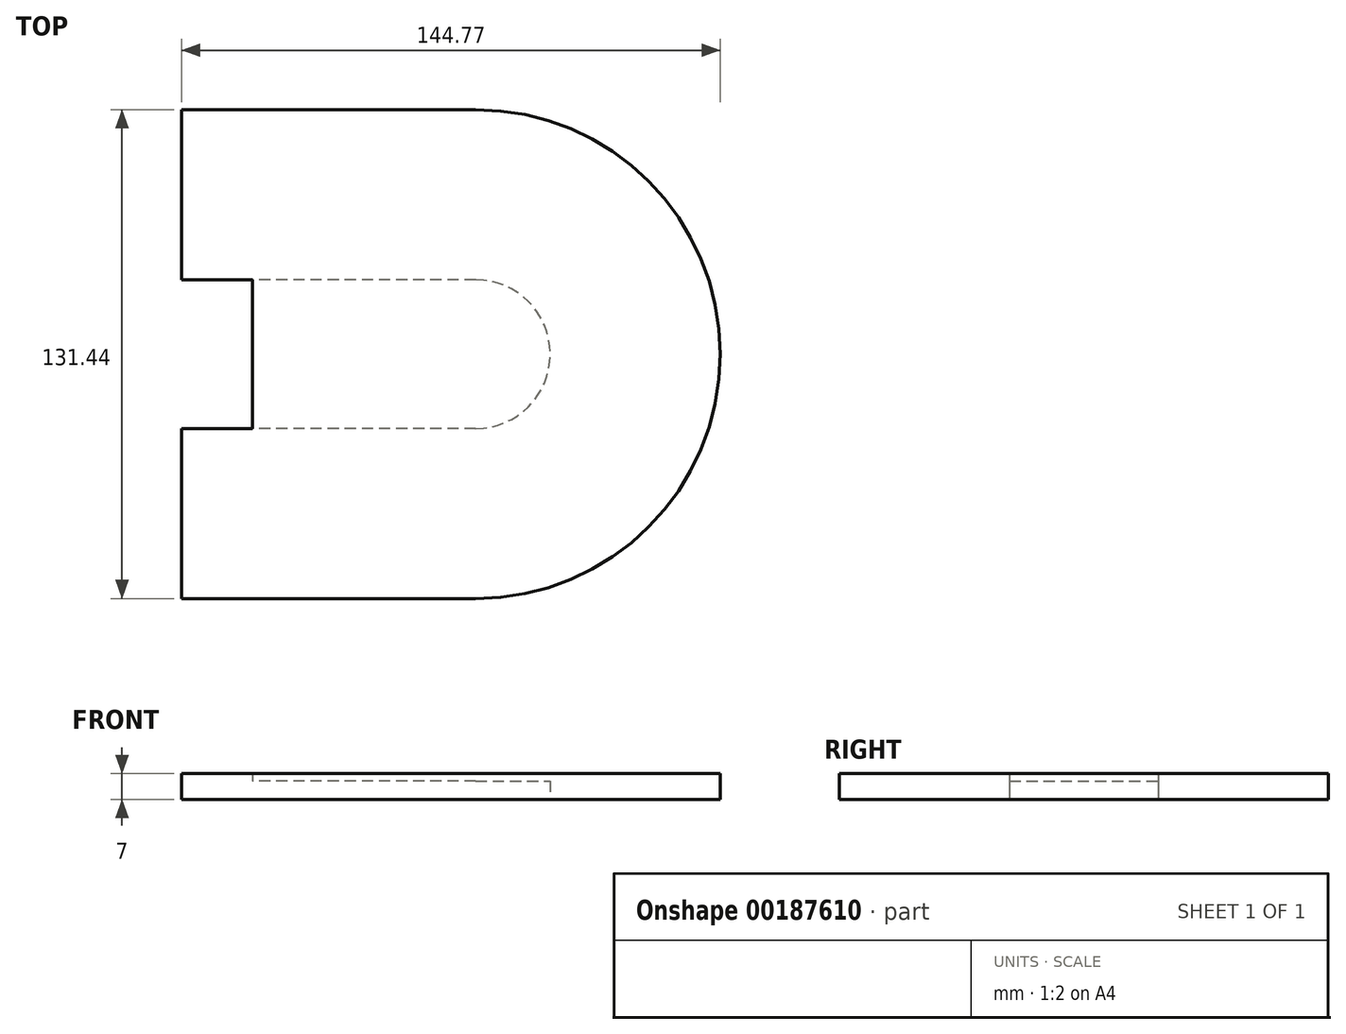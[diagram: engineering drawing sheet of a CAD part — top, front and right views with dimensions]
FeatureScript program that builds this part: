
annotation { "Feature Type Name" : "Feature", "Feature Type Description" : "" }
export const myFeature = defineFeature(function(context is Context, id is Id, definition is map)
    precondition{}
    {
        {
            var Q0;
            Q0=qCreatedBy(makeId("Top.planeOp"),FACE);
            var sketch = newSketch(context, id + "F0", { "sketchPlane" : qUnion([Q0])});
            skLineSegment(sketch, "E0.bottom", {"start": v(20, -20) * mm, "end": v(-40, -20) * mm});
            skLineSegment(sketch, "E0.top", {"start": v(20, 20) * mm, "end": v(-40, 20) * mm});
            skLineSegment(sketch, "E0.right", {"start": v(-40, -20) * mm, "end": v(-40, 20) * mm});
            skPoint(sketch, "E0.middle", {"position": v(0, 0) * mm});
            skArc(sketch, "E1", {"start": v(20, -20) * mm, "mid": v(40, 0) * mm, "end": v(20, 20) * mm});
            skPoint(sketch, "E2.orphan", {"position": v(40, 20) * mm});
            skPoint(sketch, "E3.orphan", {"position": v(40, -20) * mm});
            skLineSegment(sketch, "E4.0", {"start": v(20, 45.4) * mm, "end": v(-65.4, 45.4) * mm});
            skArc(sketch, "E4.1", {"start": v(20, -45.4) * mm, "mid": v(65.4, 0) * mm, "end": v(20, 45.4) * mm});
            skLineSegment(sketch, "E4.2", {"start": v(20, -45.4) * mm, "end": v(-65.4, -45.4) * mm});
            skLineSegment(sketch, "E4.3", {"start": v(-65.4, -45.4) * mm, "end": v(-65.4, 45.4) * mm});
            skLineSegment(sketch, "E5", {"start": v(-40, -45.4) * mm, "end": v(-40, 45.4) * mm});
            skSolve(sketch);
        }
        {
            var Q0;
            {var subQ4=sQuery(id+"F0.wireOp",EDGE,"E0.bottom");Q0=makeQuery(id+"F0.imprint","IMPRINT",FACE,{"disambiguationData":[TD([[makeQuery(id+"F0.imprint","IMPRINT",EDGE,{"derivedFrom":subQ4}),1.0]])]});}
            var Q1;
            {var subQ0=sQuery(id+"F0.wireOp",EDGE,"E0.bottom");Q1=makeQuery(id+"F0.imprint","IMPRINT",FACE,{"disambiguationData":[TD([[makeQuery(id+"F0.imprint","IMPRINT",EDGE,{"derivedFrom":subQ0}),-1.0]])]});}
            extrude(context, id + "F1", {"entities" : qUnion([Q0, Q1]), "depth" : 7 * mm});
        }
        {
            var Q0;
            {var subQ0=sQuery(id+"F0.wireOp",EDGE,"E0.bottom");Q0=makeQuery(id+"F0.imprint","IMPRINT",FACE,{"disambiguationData":[TD([[makeQuery(id+"F0.imprint","IMPRINT",EDGE,{"derivedFrom":subQ0}),-1.0]])]});}
            extrude(context, id + "F2", {"entities" : qUnion([Q0]), "operationType" : NewBodyOperationType.REMOVE, "depth" : 5 * mm});
        }
        {
            var Q0;
            Q0=makeQuery(id+"F1.opExtrude","SWEPT_FACE",FACE,{"disambiguationData":[OSD([sQuery(id+"F0.wireOp",EDGE,"E5")])]});
            var sketch = newSketch(context, id + "F3", { "sketchPlane" : qUnion([Q0])});
            skLineSegment(sketch, "E6.bottom", {"start": v(-45.4, 7) * mm, "end": v(-20, 7) * mm});
            skLineSegment(sketch, "E6.top", {"start": v(-45.4, 0) * mm, "end": v(-20, 0) * mm});
            skLineSegment(sketch, "E6.left", {"start": v(-45.4, 7) * mm, "end": v(-45.4, 0) * mm});
            skLineSegment(sketch, "E6.right", {"start": v(-20, 7) * mm, "end": v(-20, 0) * mm});
            skLineSegment(sketch, "E7.bottom", {"start": v(45.4, 7) * mm, "end": v(20, 7) * mm});
            skLineSegment(sketch, "E7.top", {"start": v(45.4, 0) * mm, "end": v(20, 0) * mm});
            skLineSegment(sketch, "E7.left", {"start": v(45.4, 7) * mm, "end": v(45.4, 0) * mm});
            skLineSegment(sketch, "E7.right", {"start": v(20, 7) * mm, "end": v(20, 0) * mm});
            skSolve(sketch);
        }
        {
            var Q0;
            Q0 = qSketchRegion(id + "F3", true);
            extrude(context, id + "F4", {"entities" : qUnion([Q0]), "operationType" : NewBodyOperationType.ADD, "depth" : 19.05 * mm});
        }
        {
            var Q0;
            Q0=makeQuery(id+"F4.boolean.opBoolean","MERGE",FACE,{"derivedFrom":[makeQuery(id+"F1.opExtrude","CAP_FACE",FACE,{"disambiguationData":[OSD([sQuery(id+"F0.wireOp",EDGE,"E4.0"),sQuery(id+"F0.wireOp",EDGE,"E4.1"),sQuery(id+"F0.wireOp",EDGE,"E4.2"),sQuery(id+"F0.wireOp",EDGE,"E5")])],"isStart":true}),makeQuery(id+"F4.opExtrude","SWEPT_FACE",FACE,{"disambiguationData":[OSD([sQuery(id+"F3.wireOp",EDGE,"E6.top")])]}),makeQuery(id+"F4.opExtrude","SWEPT_FACE",FACE,{"disambiguationData":[OSD([sQuery(id+"F3.wireOp",EDGE,"E7.top")])]})]});
            var sketch = newSketch(context, id + "F5", { "sketchPlane" : qUnion([Q0])});
            skLineSegment(sketch, "E8.0", {"start": v(20, -65.72) * mm, "end": v(-59.05, -65.72) * mm});
            skArc(sketch, "E8.1", {"start": v(20, 65.72) * mm, "mid": v(85.72, 0) * mm, "end": v(20, -65.72) * mm});
            skLineSegment(sketch, "E8.2", {"start": v(20, 65.72) * mm, "end": v(-59.05, 65.72) * mm});
            skLineSegment(sketch, "E9", {"start": v(-59.05, 45.4) * mm, "end": v(-59.05, 65.72) * mm});
            skLineSegment(sketch, "E10", {"start": v(-59.05, -65.72) * mm, "end": v(-59.05, -45.4) * mm});
            skLineSegment(sketch, "E11.0", {"start": v(20, 45.4) * mm, "end": v(-59.05, 45.4) * mm});
            skArc(sketch, "E12.0", {"start": v(20, 45.4) * mm, "mid": v(65.4, 0) * mm, "end": v(20, -45.4) * mm});
            skLineSegment(sketch, "E13.0", {"start": v(20, -45.4) * mm, "end": v(-59.05, -45.4) * mm});
            skSolve(sketch);
        }
        {
            var Q0;
            Q0=makeQuery(id+"F5.imprint","IMPRINT",FACE,{"disambiguationData":[TD([[makeQuery(id+"F5.imprint","IMPRINT",EDGE,{"derivedFrom":sQuery(id+"F5.wireOp",EDGE,"E8.0")}),-1.0]])]});
            var Q1;
            Q1=makeQuery(id+"F4.boolean.opBoolean","MERGE",FACE,{"derivedFrom":[makeQuery(id+"F1.opExtrude","CAP_FACE",FACE,{"disambiguationData":[OSD([sQuery(id+"F0.wireOp",EDGE,"E4.0"),sQuery(id+"F0.wireOp",EDGE,"E4.1"),sQuery(id+"F0.wireOp",EDGE,"E4.2"),sQuery(id+"F0.wireOp",EDGE,"E5")])],"isStart":false}),makeQuery(id+"F4.opExtrude","SWEPT_FACE",FACE,{"disambiguationData":[OSD([sQuery(id+"F3.wireOp",EDGE,"E6.bottom")])]}),makeQuery(id+"F4.opExtrude","SWEPT_FACE",FACE,{"disambiguationData":[OSD([sQuery(id+"F3.wireOp",EDGE,"E7.bottom")])]})]});
            extrude(context, id + "F6", {"entities" : qUnion([Q0]), "operationType" : NewBodyOperationType.ADD, "endBound" : BoundingType.UP_TO_SURFACE, "oppositeDirection" : true, "endBoundEntityFace" : qUnion([Q1]), "depth" : 25.4 * mm});
        }
    });
